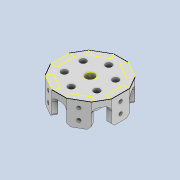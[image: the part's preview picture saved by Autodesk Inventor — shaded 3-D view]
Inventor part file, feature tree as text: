
AUTODESK INVENTOR PART (.ipt)
format: ipt  version: 2020 (Build 240168000, 168)  size: 554,496 bytes
history: native  units: mm
features: projected_geometry x16, extrude x8, sketch x8, thicken_offset x7, pattern_circular x5, fillet x3, chamfer x1
ambient origin geometry x8: Origin, YZ Plane, XZ Plane, XY Plane, X Axis, Y Axis, Z Axis, Center Point
bodies: Solid1 (feature_tree)
feature tree (48):
  extrude  "Extrusion1"  Depth=3.0mm TaperAngle=0.0deg
  extrude  "Extrusion2"  Depth=10.0mm
  pattern_circular  "Circular Pattern1"  Count=6 Angle=360.0deg
  extrude  "Extrusion4"  Depth=3.0mm TaperAngle=0.0deg
  extrude  "Extrusion5"  Depth=1.75mm
  extrude  "Extrusion6"  Depth=3.0mm
  pattern_circular  "Circular Pattern3"  [2 undecoded]
  extrude  "Extrusion7"  Depth=3.0mm TaperAngle=360.0deg
  extrude  "Extrusion8"  Depth=3.0mm
  fillet  "Fillet1"  Radius=5.0mm
  pattern_circular  "Circular Pattern4"  [2 undecoded]
  fillet  "Fillet2"  Radius=5.0mm
  pattern_circular  "Circular Pattern5"  [2 undecoded]
  chamfer  "Chamfer1"  Distance=0.5mm Angle=360.0deg
  fillet  "Fillet3"  Radius=1.0mm
  extrude  "Extrusion9"  Depth=3.0mm
  pattern_circular  "Circular Pattern6"  [2 undecoded]
  thicken_offset  "Thicken1"
  thicken_offset  "Thicken2"
  thicken_offset  "Thicken3"
  thicken_offset  "Thicken4"
  thicken_offset  "Thicken5"
  thicken_offset  "Thicken6"
  thicken_offset  "Thicken7"
  sketch  "Sketch1"  dims[d0=3.0mm d1=5.0mm d2=0.0mm]
  sketch  "Sketch2"  dims[d3=10.0mm d4=1.0mm]
  sketch  "Sketch4"  dims[d5=2.0mm]
  projected_geometry  "Projected Loop2"
  projected_geometry  "Projected Loop3"
  projected_geometry  "Projected Loop4"
  projected_geometry  "Projected Loop5"
  projected_geometry  "Projected Loop6"
  projected_geometry  "Projected Loop7"
  projected_geometry  "Projected Loop8"
  sketch  "Sketch5"  dims[d6=6.0mm]
  projected_geometry  "Projected Loop9"
  projected_geometry  "Projected Loop10"
  projected_geometry  "Projected Loop11"
  projected_geometry  "Projected Loop12"
  projected_geometry  "Projected Loop13"
  projected_geometry  "Projected Loop14"
  sketch  "Sketch6"  dims[d7=5.0mm d8=0.0mm d9=60.0mm d10=360.0deg]
  projected_geometry  "Projected Loop15"
  sketch  "Sketch7"  dims[d19=2.0mm d20=0.0mm d21=3.0mm d22=0.0mm]
  projected_geometry  "Projected Loop16"
  sketch  "Sketch8"  dims[d23=1.75mm d24=1.75mm]
  sketch  "Sketch9"  dims[d25=1.1mm d26=1.1mm d27=5.0mm d28=0.0mm d29=60.0mm d30=360.0deg d32=6.0mm d33=5.0mm d34=0.0mm d35=3.0mm d36=5.0mm d37=0.0mm d38=1.5mm d39=60.0mm d40=360.0deg d42=0.5mm d43=60.0mm d44=360.0deg d46=1.0mm d47=2.0mm d48=45.0deg d49=1.0mm d50=2.5mm d51=2.0mm d52=5.0mm d53=0.0mm d54=60.0mm d55=360.0deg d57=0.5mm d58=0.5mm d59=0.5mm d60=0.5mm d61=0.5mm d62=0.5mm d63=0.5mm d64=0.5mm d65=0.5mm d66=0.5mm d67=0.5mm d68=0.5mm d69=3.0mm d70=3.0mm]
  projected_geometry  "Projected Loop17"
note: 8 required parameter values undecoded (feature->parameter linkage not recoverable at this tier; creation-order binding heuristic only, values carry confidence <= 0.55)
